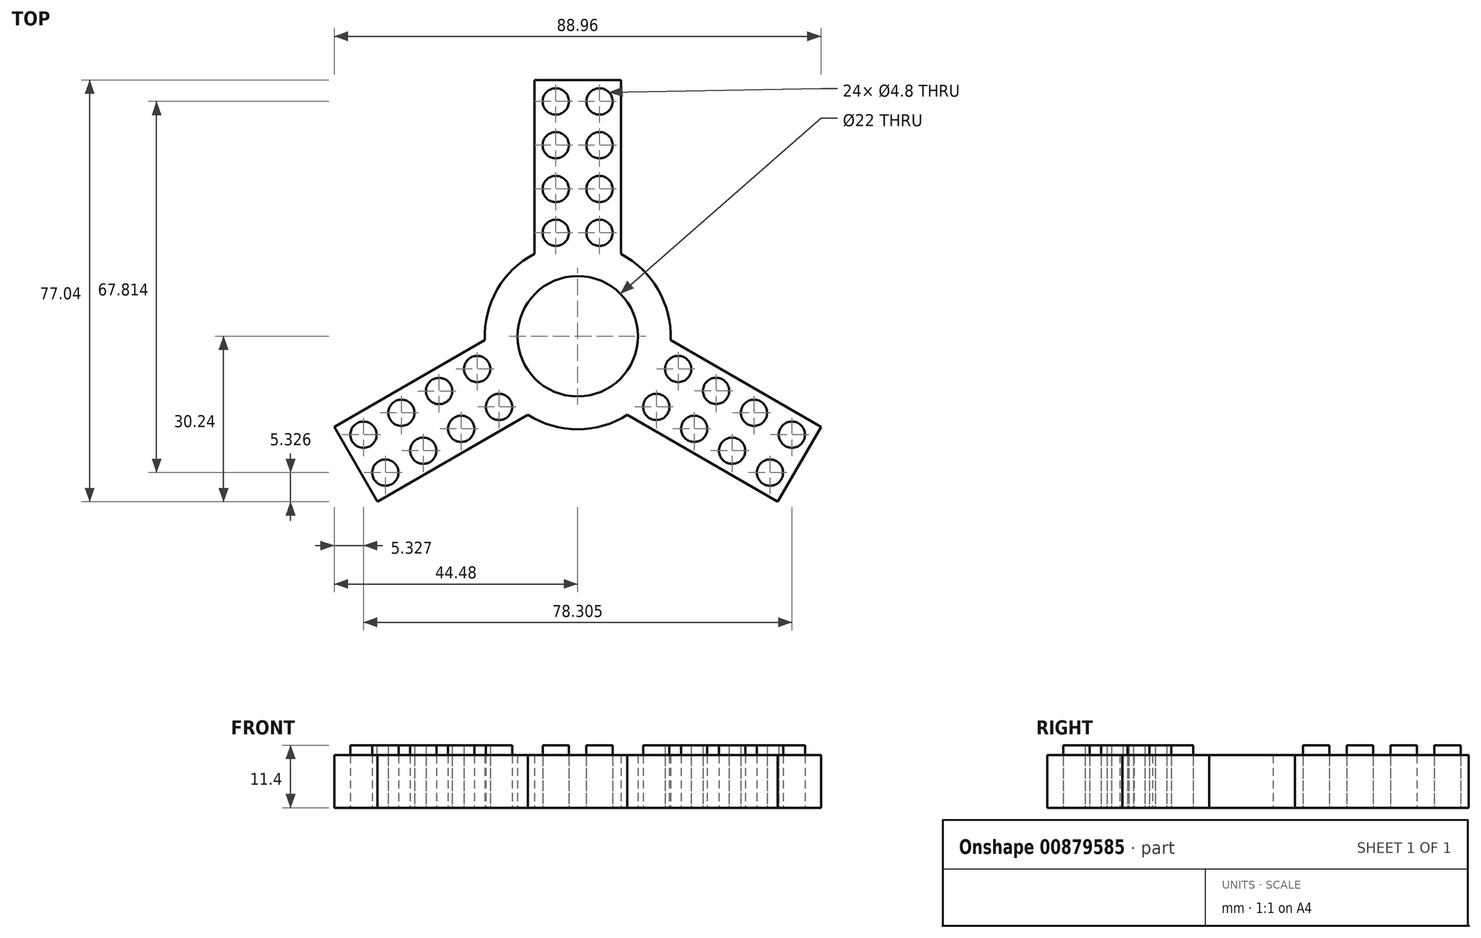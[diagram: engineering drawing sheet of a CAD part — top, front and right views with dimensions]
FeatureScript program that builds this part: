
annotation { "Feature Type Name" : "Feature", "Feature Type Description" : "" }
export const myFeature = defineFeature(function(context is Context, id is Id, definition is map)
    precondition{}
    {
        {
            var Q0;
            Q0=qCreatedBy(makeId("Top.planeOp"),FACE);
            var sketch = newSketch(context, id + "F0", { "sketchPlane" : qUnion([Q0])});
            skCircle(sketch, "E0", {"center": v(0, 0) * mm, "radius": 11 * mm});
            skArc(sketch, "E1", {"start": v(-7.9, 15.05) * mm, "mid": v(-14.72, 8.5) * mm, "end": v(-16.99, -0.68) * mm});
            skArc(sketch, "E2.cCircle", {"start": v(-7.9, 15.05) * mm, "mid": v(-14.72, 8.5) * mm, "end": v(-16.99, -0.68) * mm, "construction": true});
            skLineSegment(sketch, "E3", {"start": v(-7.9, 15) * mm, "end": v(-7.9, 46.8) * mm});
            skLineSegment(sketch, "E4", {"start": v(7.9, 15) * mm, "end": v(7.9, 46.8) * mm});
            skLineSegment(sketch, "E5", {"start": v(-16.94, -0.66) * mm, "end": v(-44.48, -16.56) * mm});
            skLineSegment(sketch, "E6", {"start": v(-9.04, -14.34) * mm, "end": v(-36.58, -30.24) * mm});
            skLineSegment(sketch, "E7", {"start": v(16.94, -0.66) * mm, "end": v(44.48, -16.56) * mm});
            skLineSegment(sketch, "E8", {"start": v(9.04, -14.34) * mm, "end": v(36.58, -30.24) * mm});
            skLineSegment(sketch, "E9", {"start": v(-7.9, 46.8) * mm, "end": v(7.9, 46.8) * mm});
            skLineSegment(sketch, "E10", {"start": v(-44.48, -16.56) * mm, "end": v(-36.58, -30.24) * mm});
            skLineSegment(sketch, "E11", {"start": v(36.58, -30.24) * mm, "end": v(44.48, -16.56) * mm});
            skArc(sketch, "E12.trimOffspring", {"start": v(-9.09, -14.37) * mm, "mid": v(0, -17) * mm, "end": v(9.09, -14.37) * mm, "construction": true});
            skArc(sketch, "E13.trimOffspring", {"start": v(-9.09, -14.37) * mm, "mid": v(0, -17) * mm, "end": v(9.09, -14.37) * mm});
            skArc(sketch, "E14.trimOffspring", {"start": v(16.99, -0.68) * mm, "mid": v(14.72, 8.5) * mm, "end": v(7.9, 15.05) * mm, "construction": true});
            skArc(sketch, "E15.trimOffspring", {"start": v(16.99, -0.68) * mm, "mid": v(14.72, 8.5) * mm, "end": v(7.9, 15.05) * mm});
            skCircle(sketch, "E16", {"center": v(4, 42.9) * mm, "radius": 2.4 * mm});
            skCircle(sketch, "E17", {"center": v(-4, 42.9) * mm, "radius": 2.4 * mm});
            skCircle(sketch, "E18", {"center": v(4, 34.9) * mm, "radius": 2.4 * mm});
            skCircle(sketch, "E19", {"center": v(-4, 34.9) * mm, "radius": 2.4 * mm});
            skCircle(sketch, "E20", {"center": v(4, 26.9) * mm, "radius": 2.4 * mm});
            skCircle(sketch, "E21", {"center": v(-4, 26.9) * mm, "radius": 2.4 * mm});
            skCircle(sketch, "E22", {"center": v(4, 18.9) * mm, "radius": 2.4 * mm});
            skCircle(sketch, "E23", {"center": v(-4, 18.9) * mm, "radius": 2.4 * mm});
            skCircle(sketch, "E24", {"center": v(18.37, -5.99) * mm, "radius": 2.4 * mm});
            skCircle(sketch, "E25", {"center": v(25.3, -9.99) * mm, "radius": 2.4 * mm});
            skCircle(sketch, "E26", {"center": v(32.22, -13.99) * mm, "radius": 2.4 * mm});
            skCircle(sketch, "E27", {"center": v(39.15, -17.99) * mm, "radius": 2.4 * mm});
            skCircle(sketch, "E28", {"center": v(35.15, -24.91) * mm, "radius": 2.4 * mm});
            skCircle(sketch, "E29", {"center": v(28.22, -20.91) * mm, "radius": 2.4 * mm});
            skCircle(sketch, "E30", {"center": v(21.3, -16.91) * mm, "radius": 2.4 * mm});
            skCircle(sketch, "E31", {"center": v(14.37, -12.91) * mm, "radius": 2.4 * mm});
            skCircle(sketch, "E32", {"center": v(-18.37, -5.99) * mm, "radius": 2.4 * mm});
            skCircle(sketch, "E33", {"center": v(-25.33, -10) * mm, "radius": 2.4 * mm});
            skCircle(sketch, "E34", {"center": v(-32.22, -13.99) * mm, "radius": 2.4 * mm});
            skCircle(sketch, "E35", {"center": v(-39.15, -17.99) * mm, "radius": 2.4 * mm});
            skCircle(sketch, "E36", {"center": v(-35.15, -24.91) * mm, "radius": 2.4 * mm});
            skCircle(sketch, "E37", {"center": v(-28.22, -20.91) * mm, "radius": 2.4 * mm});
            skCircle(sketch, "E38", {"center": v(-21.3, -16.91) * mm, "radius": 2.4 * mm});
            skCircle(sketch, "E39", {"center": v(-14.37, -12.91) * mm, "radius": 2.4 * mm});
            skLineSegment(sketch, "E40.0", {"start": v(0, 15) * mm, "end": v(0, 46.8) * mm});
            skLineSegment(sketch, "E41.0", {"start": v(13, -7.5) * mm, "end": v(40.53, -23.4) * mm});
            skLineSegment(sketch, "E42.0", {"start": v(-13, -7.5) * mm, "end": v(-40.53, -23.4) * mm});
            skSolve(sketch);
        }
        {
            var Q0;
            Q0=makeQuery(id+"F0.imprint","IMPRINT",FACE,{"disambiguationData":[TD([[makeQuery(id+"F0.imprint","IMPRINT",EDGE,{"derivedFrom":sQuery(id+"F0.wireOp",EDGE,"E18")}),1.0]])]});
            var Q1;
            Q1=makeQuery(id+"F0.imprint","IMPRINT",FACE,{"disambiguationData":[TD([[makeQuery(id+"F0.imprint","IMPRINT",EDGE,{"derivedFrom":sQuery(id+"F0.wireOp",EDGE,"E17")}),1.0]])]});
            var Q2;
            Q2=makeQuery(id+"F0.imprint","IMPRINT",FACE,{"disambiguationData":[TD([[makeQuery(id+"F0.imprint","IMPRINT",EDGE,{"derivedFrom":sQuery(id+"F0.wireOp",EDGE,"E16")}),1.0]])]});
            var Q3;
            Q3=makeQuery(id+"F0.imprint","IMPRINT",FACE,{"disambiguationData":[TD([[makeQuery(id+"F0.imprint","IMPRINT",EDGE,{"derivedFrom":sQuery(id+"F0.wireOp",EDGE,"E19")}),1.0]])]});
            var Q4;
            Q4=makeQuery(id+"F0.imprint","IMPRINT",FACE,{"disambiguationData":[TD([[makeQuery(id+"F0.imprint","IMPRINT",EDGE,{"derivedFrom":sQuery(id+"F0.wireOp",EDGE,"E21")}),1.0]])]});
            var Q5;
            Q5=makeQuery(id+"F0.imprint","IMPRINT",FACE,{"disambiguationData":[TD([[makeQuery(id+"F0.imprint","IMPRINT",EDGE,{"derivedFrom":sQuery(id+"F0.wireOp",EDGE,"E20")}),1.0]])]});
            var Q6;
            Q6=makeQuery(id+"F0.imprint","IMPRINT",FACE,{"disambiguationData":[TD([[makeQuery(id+"F0.imprint","IMPRINT",EDGE,{"derivedFrom":sQuery(id+"F0.wireOp",EDGE,"E23")}),1.0]])]});
            var Q7;
            Q7=makeQuery(id+"F0.imprint","IMPRINT",FACE,{"disambiguationData":[TD([[makeQuery(id+"F0.imprint","IMPRINT",EDGE,{"derivedFrom":sQuery(id+"F0.wireOp",EDGE,"E22")}),1.0]])]});
            var Q8;
            Q8=makeQuery(id+"F0.imprint","IMPRINT",FACE,{"disambiguationData":[TD([[makeQuery(id+"F0.imprint","IMPRINT",EDGE,{"derivedFrom":sQuery(id+"F0.wireOp",EDGE,"E36")}),1.0]])]});
            var Q9;
            Q9=makeQuery(id+"F0.imprint","IMPRINT",FACE,{"disambiguationData":[TD([[makeQuery(id+"F0.imprint","IMPRINT",EDGE,{"derivedFrom":sQuery(id+"F0.wireOp",EDGE,"E35")}),1.0]])]});
            var Q10;
            Q10=makeQuery(id+"F0.imprint","IMPRINT",FACE,{"disambiguationData":[TD([[makeQuery(id+"F0.imprint","IMPRINT",EDGE,{"derivedFrom":sQuery(id+"F0.wireOp",EDGE,"E34")}),1.0]])]});
            var Q11;
            Q11=makeQuery(id+"F0.imprint","IMPRINT",FACE,{"disambiguationData":[TD([[makeQuery(id+"F0.imprint","IMPRINT",EDGE,{"derivedFrom":sQuery(id+"F0.wireOp",EDGE,"E33")}),1.0]])]});
            var Q12;
            Q12=makeQuery(id+"F0.imprint","IMPRINT",FACE,{"disambiguationData":[TD([[makeQuery(id+"F0.imprint","IMPRINT",EDGE,{"derivedFrom":sQuery(id+"F0.wireOp",EDGE,"E32")}),1.0]])]});
            var Q13;
            Q13=makeQuery(id+"F0.imprint","IMPRINT",FACE,{"disambiguationData":[TD([[makeQuery(id+"F0.imprint","IMPRINT",EDGE,{"derivedFrom":sQuery(id+"F0.wireOp",EDGE,"E39")}),1.0]])]});
            var Q14;
            Q14=makeQuery(id+"F0.imprint","IMPRINT",FACE,{"disambiguationData":[TD([[makeQuery(id+"F0.imprint","IMPRINT",EDGE,{"derivedFrom":sQuery(id+"F0.wireOp",EDGE,"E38")}),1.0]])]});
            var Q15;
            Q15=makeQuery(id+"F0.imprint","IMPRINT",FACE,{"disambiguationData":[TD([[makeQuery(id+"F0.imprint","IMPRINT",EDGE,{"derivedFrom":sQuery(id+"F0.wireOp",EDGE,"E37")}),1.0]])]});
            var Q16;
            Q16=makeQuery(id+"F0.imprint","IMPRINT",FACE,{"disambiguationData":[TD([[makeQuery(id+"F0.imprint","IMPRINT",EDGE,{"derivedFrom":sQuery(id+"F0.wireOp",EDGE,"E31")}),1.0]])]});
            var Q17;
            Q17=makeQuery(id+"F0.imprint","IMPRINT",FACE,{"disambiguationData":[TD([[makeQuery(id+"F0.imprint","IMPRINT",EDGE,{"derivedFrom":sQuery(id+"F0.wireOp",EDGE,"E24")}),1.0]])]});
            var Q18;
            Q18=makeQuery(id+"F0.imprint","IMPRINT",FACE,{"disambiguationData":[TD([[makeQuery(id+"F0.imprint","IMPRINT",EDGE,{"derivedFrom":sQuery(id+"F0.wireOp",EDGE,"E25")}),1.0]])]});
            var Q19;
            Q19=makeQuery(id+"F0.imprint","IMPRINT",FACE,{"disambiguationData":[TD([[makeQuery(id+"F0.imprint","IMPRINT",EDGE,{"derivedFrom":sQuery(id+"F0.wireOp",EDGE,"E26")}),1.0]])]});
            var Q20;
            Q20=makeQuery(id+"F0.imprint","IMPRINT",FACE,{"disambiguationData":[TD([[makeQuery(id+"F0.imprint","IMPRINT",EDGE,{"derivedFrom":sQuery(id+"F0.wireOp",EDGE,"E27")}),1.0]])]});
            var Q21;
            Q21=makeQuery(id+"F0.imprint","IMPRINT",FACE,{"disambiguationData":[TD([[makeQuery(id+"F0.imprint","IMPRINT",EDGE,{"derivedFrom":sQuery(id+"F0.wireOp",EDGE,"E28")}),1.0]])]});
            var Q22;
            Q22=makeQuery(id+"F0.imprint","IMPRINT",FACE,{"disambiguationData":[TD([[makeQuery(id+"F0.imprint","IMPRINT",EDGE,{"derivedFrom":sQuery(id+"F0.wireOp",EDGE,"E29")}),1.0]])]});
            var Q23;
            Q23=makeQuery(id+"F0.imprint","IMPRINT",FACE,{"disambiguationData":[TD([[makeQuery(id+"F0.imprint","IMPRINT",EDGE,{"derivedFrom":sQuery(id+"F0.wireOp",EDGE,"E30")}),1.0]])]});
            extrude(context, id + "F1", {"entities" : qUnion([Q0, Q1, Q2, Q3, Q4, Q5, Q6, Q7, Q8, Q9, Q10, Q11, Q12, Q13, Q14, Q15, Q16, Q17, Q18, Q19, Q20, Q21, Q22, Q23]), "depth" : 11.4 * mm, "offsetDistance" : 25 * mm});
        }
        {
            var Q0;
            Q0=makeQuery(id+"F0.imprint","IMPRINT",FACE,{"disambiguationData":[TD([[makeQuery(id+"F0.imprint","IMPRINT",EDGE,{"derivedFrom":sQuery(id+"F0.wireOp",EDGE,"E0")}),-1.0]])]});
            extrude(context, id + "F2", {"entities" : qUnion([Q0]), "depth" : 9.6 * mm, "offsetDistance" : 25 * mm});
        }
    });
